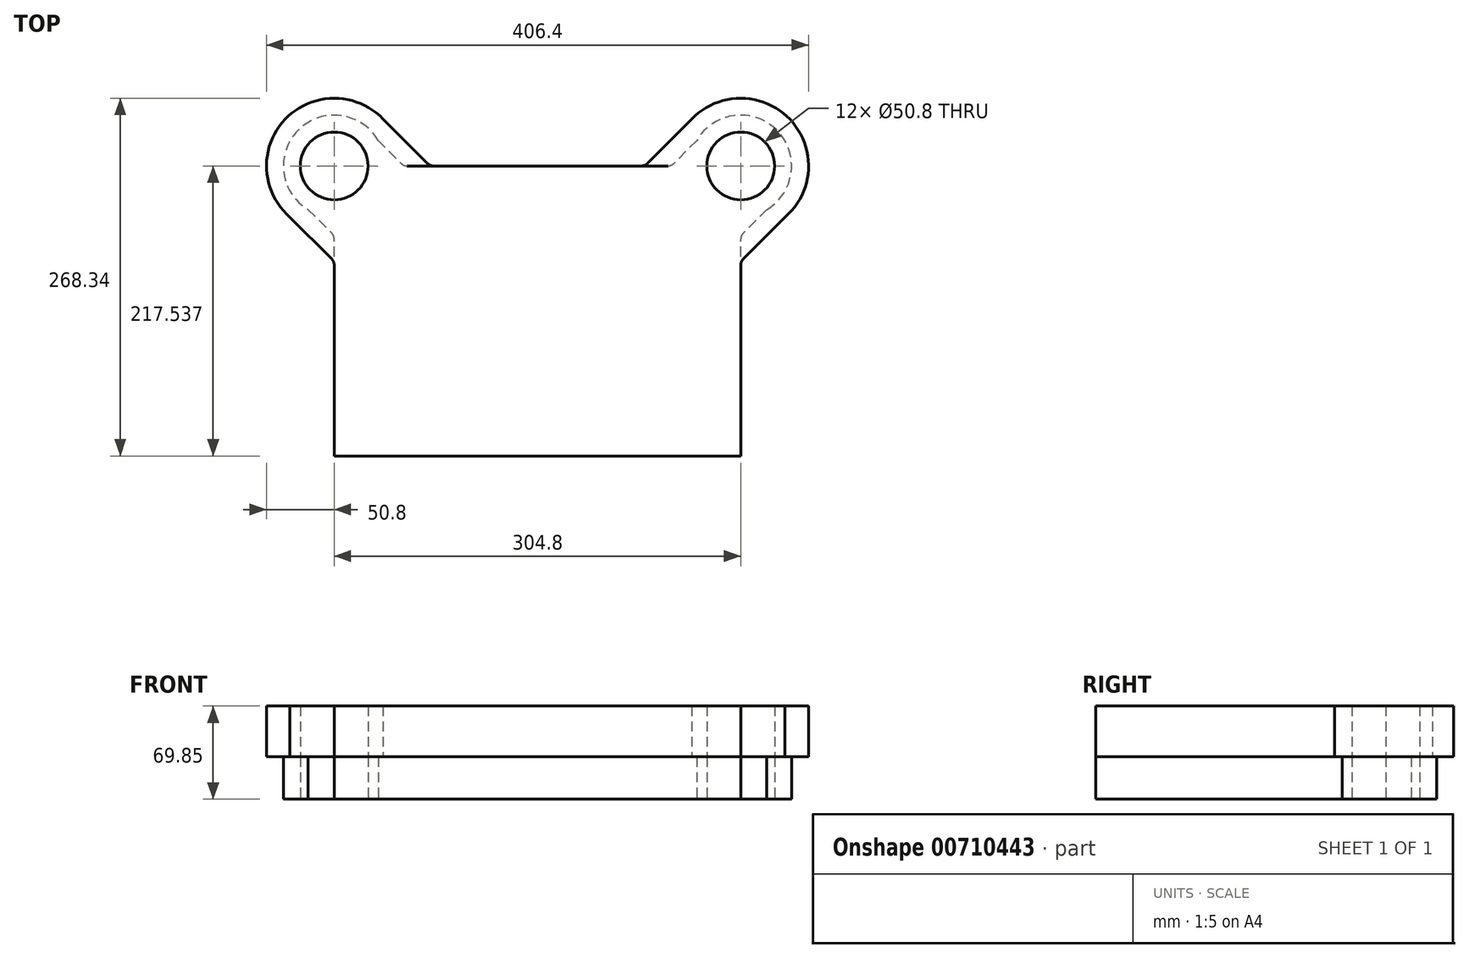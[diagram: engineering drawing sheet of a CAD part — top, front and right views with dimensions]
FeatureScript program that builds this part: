
annotation { "Feature Type Name" : "Feature", "Feature Type Description" : "" }
export const myFeature = defineFeature(function(context is Context, id is Id, definition is map)
    precondition{}
    {
        {
            var Q0;
            Q0=qCreatedBy(makeId("Top.planeOp"),FACE);
            var sketch = newSketch(context, id + "F0", { "sketchPlane" : qUnion([Q0])});
            skLineSegment(sketch, "E0.bottom", {"start": v(-152.4, -108.77) * mm, "end": v(152.4, -108.77) * mm});
            skLineSegment(sketch, "E0.top", {"start": v(-97.72, 108.77) * mm, "end": v(97.72, 108.77) * mm});
            skLineSegment(sketch, "E0.left", {"start": v(-152.4, -108.77) * mm, "end": v(-152.4, 70.67) * mm});
            skLineSegment(sketch, "E0.right", {"start": v(152.4, -108.77) * mm, "end": v(152.4, 53.9) * mm});
            skPoint(sketch, "E0.middle", {"position": v(0, 0) * mm});
            skCircle(sketch, "E1", {"center": v(-152.4, 108.77) * mm, "radius": 38.1 * mm});
            skCircle(sketch, "E2", {"center": v(152.4, 108.77) * mm, "radius": 38.1 * mm});
            skPoint(sketch, "E3", {"position": v(-119.4, 127.82) * mm});
            skPoint(sketch, "E4.MirrorP", {"position": v(119.4, 127.82) * mm});
            skLineSegment(sketch, "E5", {"start": v(-119.4, 127.82) * mm, "end": v(-102.21, 110.63) * mm});
            skLineSegment(sketch, "E6.MirrorCS", {"start": v(119.4, 127.82) * mm, "end": v(102.21, 110.63) * mm});
            skPoint(sketch, "E7.newPointB", {"position": v(100.35, 108.77) * mm});
            skArc(sketch, "E7.filletArc", {"start": v(97.72, 108.77) * mm, "mid": v(100.15, 109.25) * mm, "end": v(102.21, 110.63) * mm});
            skPoint(sketch, "E8.newPointA", {"position": v(-100.35, 108.77) * mm});
            skArc(sketch, "E8.filletArc", {"start": v(-102.21, 110.63) * mm, "mid": v(-100.15, 109.25) * mm, "end": v(-97.72, 108.77) * mm});
            skLineSegment(sketch, "E9", {"start": v(171.9, 76.04) * mm, "end": v(154.26, 58.4) * mm});
            skArc(sketch, "E10.filletArc", {"start": v(154.26, 58.4) * mm, "mid": v(152.88, 56.33) * mm, "end": v(152.4, 53.9) * mm});
            skLineSegment(sketch, "E11.MirrorCS", {"start": v(-171.9, 76.04) * mm, "end": v(-154.26, 58.4) * mm});
            skArc(sketch, "E12.MirrorCS", {"start": v(-154.26, 58.4) * mm, "mid": v(-152.88, 56.33) * mm, "end": v(-152.4, 53.9) * mm});
            skCircle(sketch, "E13", {"center": v(-152.4, 108.77) * mm, "radius": 25.4 * mm});
            skCircle(sketch, "E14", {"center": v(152.4, 108.77) * mm, "radius": 25.4 * mm});
            skSolve(sketch);
        }
        {
            var Q0;
            {var subQ7=sQuery(id+"F0.wireOp",EDGE,"E0.bottom");Q0=makeQuery(id+"F0.imprint","IMPRINT",FACE,{"disambiguationData":[TD([[makeQuery(id+"F0.imprint","IMPRINT",EDGE,{"derivedFrom":subQ7}),1.0]])]});}
            var Q1;
            Q1=makeQuery(id+"F0.imprint","IMPRINT",FACE,{"disambiguationData":[TD([[makeQuery(id+"F0.imprint","IMPRINT",EDGE,{"derivedFrom":sQuery(id+"F0.wireOp",EDGE,"E13")}),-1.0]])]});
            var Q2;
            Q2=makeQuery(id+"F0.imprint","IMPRINT",FACE,{"disambiguationData":[TD([[makeQuery(id+"F0.imprint","IMPRINT",EDGE,{"derivedFrom":sQuery(id+"F0.wireOp",EDGE,"E14")}),-1.0]])]});
            var Q3;
            {var subQ4=sQuery(id+"F0.wireOp",EDGE,"E11.MirrorCS");Q3=makeQuery(id+"F0.imprint","IMPRINT",FACE,{"disambiguationData":[TD([[makeQuery(id+"F0.imprint","IMPRINT",EDGE,{"derivedFrom":subQ4}),1.0]])]});}
            extrude(context, id + "F1", {"entities" : qUnion([Q0, Q1, Q2, Q3]), "depth" : 31.75 * mm, "offsetDistance" : 25.4 * mm});
        }
        {
            var Q0;
            Q0=makeQuery(id+"F1.opExtrude","SWEPT_BODY",BODY,{"disambiguationData":[OSD([sQuery(id+"F0.wireOp",EDGE,"E0.bottom"),sQuery(id+"F0.wireOp",EDGE,"E0.top"),sQuery(id+"F0.wireOp",EDGE,"E0.left"),sQuery(id+"F0.wireOp",EDGE,"E0.right"),sQuery(id+"F0.wireOp",EDGE,"E1"),sQuery(id+"F0.wireOp",EDGE,"E2"),sQuery(id+"F0.wireOp",EDGE,"E5"),sQuery(id+"F0.wireOp",EDGE,"E6.MirrorCS"),sQuery(id+"F0.wireOp",EDGE,"E7.filletArc"),sQuery(id+"F0.wireOp",EDGE,"E8.filletArc"),sQuery(id+"F0.wireOp",EDGE,"E9"),sQuery(id+"F0.wireOp",EDGE,"E10.filletArc"),sQuery(id+"F0.wireOp",EDGE,"E11.MirrorCS"),sQuery(id+"F0.wireOp",EDGE,"E12.MirrorCS"),sQuery(id+"F0.wireOp",EDGE,"E13"),sQuery(id+"F0.wireOp",EDGE,"E14")])]});
            transform(context, id + "F2", {"entities" : qUnion([Q0]), "transformType" : TransformType.TRANSLATION_3D, "dx" : 0 * mm, "dy" : 0 * mm, "dz" : 0 * mm, "makeCopy" : true});
        }
        {
            var Q0;
            Q0=makeQuery(id+"F2.opPattern","COPY",BODY,{"derivedFrom":makeQuery(id+"F1.opExtrude","SWEPT_BODY",BODY,{"disambiguationData":[OSD([sQuery(id+"F0.wireOp",EDGE,"E0.bottom"),sQuery(id+"F0.wireOp",EDGE,"E0.top"),sQuery(id+"F0.wireOp",EDGE,"E0.left"),sQuery(id+"F0.wireOp",EDGE,"E0.right"),sQuery(id+"F0.wireOp",EDGE,"E1"),sQuery(id+"F0.wireOp",EDGE,"E2"),sQuery(id+"F0.wireOp",EDGE,"E5"),sQuery(id+"F0.wireOp",EDGE,"E6.MirrorCS"),sQuery(id+"F0.wireOp",EDGE,"E7.filletArc"),sQuery(id+"F0.wireOp",EDGE,"E8.filletArc"),sQuery(id+"F0.wireOp",EDGE,"E9"),sQuery(id+"F0.wireOp",EDGE,"E10.filletArc"),sQuery(id+"F0.wireOp",EDGE,"E11.MirrorCS"),sQuery(id+"F0.wireOp",EDGE,"E12.MirrorCS"),sQuery(id+"F0.wireOp",EDGE,"E13"),sQuery(id+"F0.wireOp",EDGE,"E14")])]}),"instanceName":"1"});
            deleteBodies(context, id + "F3", {"entities" : qUnion([Q0])});
        }
        {
            var Q0;
            Q0=makeQuery(id+"F1.opExtrude","CAP_FACE",FACE,{"disambiguationData":[OSD([sQuery(id+"F0.wireOp",EDGE,"E0.bottom"),sQuery(id+"F0.wireOp",EDGE,"E0.top"),sQuery(id+"F0.wireOp",EDGE,"E0.left"),sQuery(id+"F0.wireOp",EDGE,"E0.right"),sQuery(id+"F0.wireOp",EDGE,"E1"),sQuery(id+"F0.wireOp",EDGE,"E2"),sQuery(id+"F0.wireOp",EDGE,"E5"),sQuery(id+"F0.wireOp",EDGE,"E6.MirrorCS"),sQuery(id+"F0.wireOp",EDGE,"E7.filletArc"),sQuery(id+"F0.wireOp",EDGE,"E8.filletArc"),sQuery(id+"F0.wireOp",EDGE,"E9"),sQuery(id+"F0.wireOp",EDGE,"E10.filletArc"),sQuery(id+"F0.wireOp",EDGE,"E11.MirrorCS"),sQuery(id+"F0.wireOp",EDGE,"E12.MirrorCS"),sQuery(id+"F0.wireOp",EDGE,"E13"),sQuery(id+"F0.wireOp",EDGE,"E14")])],"isStart":false});
            var sketch = newSketch(context, id + "F4", { "sketchPlane" : qUnion([Q0])});
            skCircle(sketch, "E15", {"center": v(-152.4, 108.77) * mm, "radius": 25.4 * mm});
            skCircle(sketch, "E16", {"center": v(152.4, 108.77) * mm, "radius": 25.4 * mm});
            skLineSegment(sketch, "E17.bottom", {"start": v(152.4, -108.77) * mm, "end": v(-152.4, -108.77) * mm});
            skLineSegment(sketch, "E17.top", {"start": v(77.94, 108.77) * mm, "end": v(-77.94, 108.77) * mm});
            skLineSegment(sketch, "E17.left", {"start": v(152.4, -108.77) * mm, "end": v(152.4, 34.49) * mm});
            skLineSegment(sketch, "E17.right", {"start": v(-152.4, -108.77) * mm, "end": v(-152.4, 34.49) * mm});
            skPoint(sketch, "E17.middle", {"position": v(0, 0) * mm});
            skArc(sketch, "E18", {"start": v(-115.71, 143.9) * mm, "mid": v(-189.24, 143.75) * mm, "end": v(-185.6, 70.31) * mm});
            skArc(sketch, "E19", {"start": v(185.6, 70.31) * mm, "mid": v(189.24, 143.75) * mm, "end": v(115.71, 143.9) * mm});
            skLineSegment(sketch, "E20", {"start": v(-117.26, 145.46) * mm, "end": v(-82.43, 110.63) * mm});
            skArc(sketch, "E21.filletArc", {"start": v(-82.43, 110.63) * mm, "mid": v(-80.37, 109.25) * mm, "end": v(-77.94, 108.77) * mm});
            skLineSegment(sketch, "E22.MirrorCS", {"start": v(117.26, 145.46) * mm, "end": v(82.43, 110.63) * mm});
            skArc(sketch, "E23.MirrorCS", {"start": v(82.43, 110.63) * mm, "mid": v(80.37, 109.25) * mm, "end": v(77.94, 108.77) * mm});
            skLineSegment(sketch, "E24", {"start": v(-190.85, 75.57) * mm, "end": v(-154.26, 38.98) * mm});
            skArc(sketch, "E25.filletArc", {"start": v(-152.4, 34.49) * mm, "mid": v(-152.88, 36.92) * mm, "end": v(-154.26, 38.98) * mm});
            skLineSegment(sketch, "E26.MirrorCS", {"start": v(190.85, 75.57) * mm, "end": v(154.26, 38.98) * mm});
            skArc(sketch, "E27.MirrorCS", {"start": v(152.4, 34.49) * mm, "mid": v(152.88, 36.92) * mm, "end": v(154.26, 38.98) * mm});
            skSolve(sketch);
        }
        {
            var Q0;
            Q0 = qSketchRegion(id + "F4", true);
            extrude(context, id + "F5", {"entities" : qUnion([Q0]), "depth" : 38.1 * mm, "offsetDistance" : 25.4 * mm});
        }
    });
